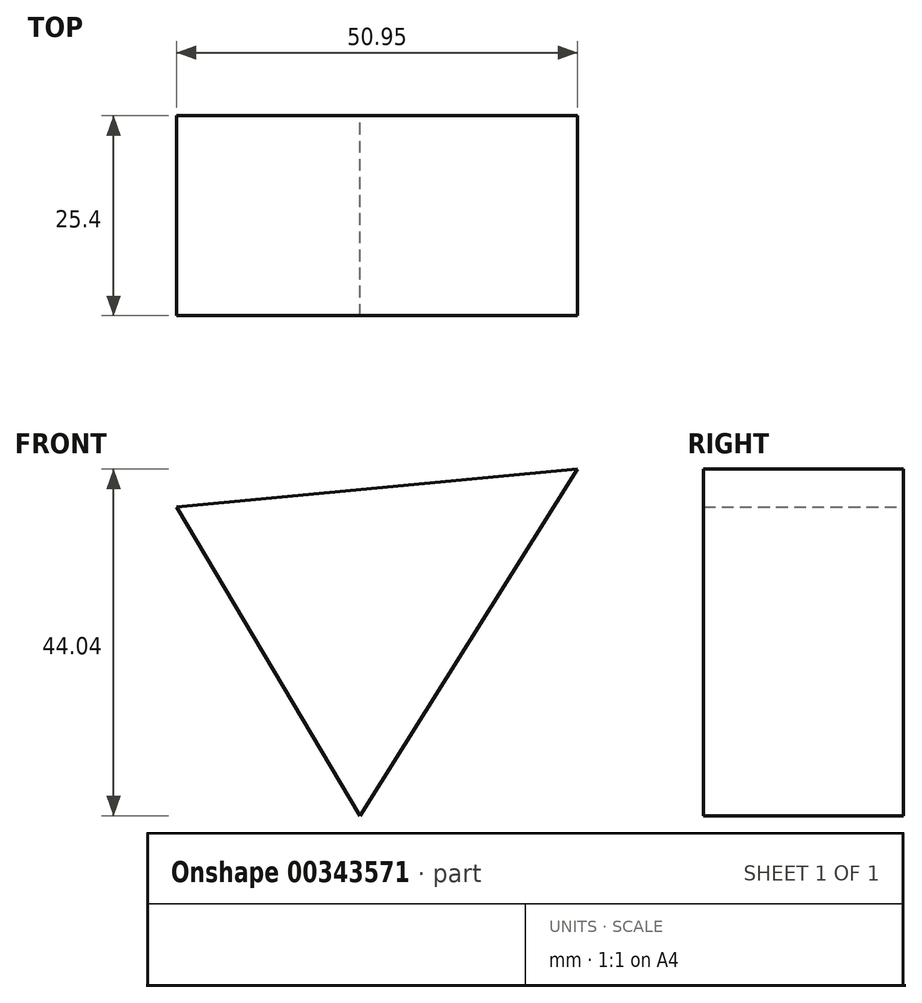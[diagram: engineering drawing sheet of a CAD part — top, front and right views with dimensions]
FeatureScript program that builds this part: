
annotation { "Feature Type Name" : "Feature", "Feature Type Description" : "" }
export const myFeature = defineFeature(function(context is Context, id is Id, definition is map)
    precondition{}
    {
        {
            var Q0;
            Q0=qCreatedBy(makeId("Front.planeOp"),FACE);
            var sketch = newSketch(context, id + "F0", { "sketchPlane" : qUnion([Q0])});
            skLineSegment(sketch, "E0", {"start": v(-2, 0) * mm, "end": v(-25.31, 39.21) * mm});
            skLineSegment(sketch, "E1", {"start": v(-25.31, 39.21) * mm, "end": v(25.64, 44.04) * mm});
            skLineSegment(sketch, "E2", {"start": v(25.64, 44.04) * mm, "end": v(-2, 0) * mm});
            skSolve(sketch);
        }
        {
            var Q0;
            Q0=makeQuery(id+"F0.imprint","IMPRINT",FACE,{"disambiguationData":[TD([[makeQuery(id+"F0.imprint","IMPRINT",EDGE,{"derivedFrom":sQuery(id+"F0.wireOp",EDGE,"E0")}),-1.0]])]});
            extrude(context, id + "F1", {"entities" : qUnion([Q0]), "depth" : 25.4 * mm});
        }
    });
